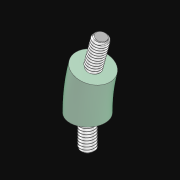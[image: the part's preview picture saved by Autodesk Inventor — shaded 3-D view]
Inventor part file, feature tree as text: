
AUTODESK INVENTOR PART (.ipt)
format: ipt  version: 2021.3 (Build 253353010, 353A)  size: 598,528 bytes
history: native  units: in
note: dims shown in document units (in); Inventor stores cm internally (conversion verified against a paired STEP export)
features: sketch x8, other x7, extrude x2
ambient origin geometry x8: Origin, YZ Plane, XZ Plane, XY Plane, X Axis, Y Axis, Z Axis, Center Point
bodies: Solid1 (feature_tree), Body (feature_tree)
feature tree (17):
  other  "Rubber Link Bent"
  other  "Table"
  extrude  "Top"  Depth=0.5in
  extrude  "Bottom"  TaperAngle=0.0deg  [1 undecoded]
  other  "Work Axis1"
  other  "Top Thread"
  other  "Bottom Thread"
  other  "Taper Top"
  other  "Taper Bottom"
  sketch  "Sketch1"  dims[d0=0.41in d2=0.5in]
  sketch  "Sketch2"  dims[d3=0.25in d4=0.0in d5=0.0in]
  sketch  "Sketch3"  dims[d6=0.123in]
  sketch  "Sketch4"  dims[d7=0.365in d8=0.0in]
  sketch  "Sketch5"  dims[d9=0.123in]
  sketch  "Sketch6"  dims[d10=0.365in d11=0.0in]
  sketch  "Sketch7"  dims[d12=0.004in]
  sketch  "Sketch8"  dims[d13=60.0deg d14=0.021in d15=0.003in d16=0.031in d17=0.415in d18=0.3937in d19=0.0in d20=90.0deg d21=90.0deg d22=0.0in d23=0.0in d24=0.004in d25=0.021in d26=60.0deg d27=0.003in d28=0.031in d29=0.415in d30=0.3937in d31=0.0in d32=90.0deg d33=90.0deg d34=0.0in d35=0.0in d37=0.059in d38=135.0deg d39=90.0deg d40=0.059in d41=135.0deg d42=90.0deg]
note: 1 required parameter value undecoded (feature->parameter linkage not recoverable at this tier; creation-order binding heuristic only, values carry confidence <= 0.55)
